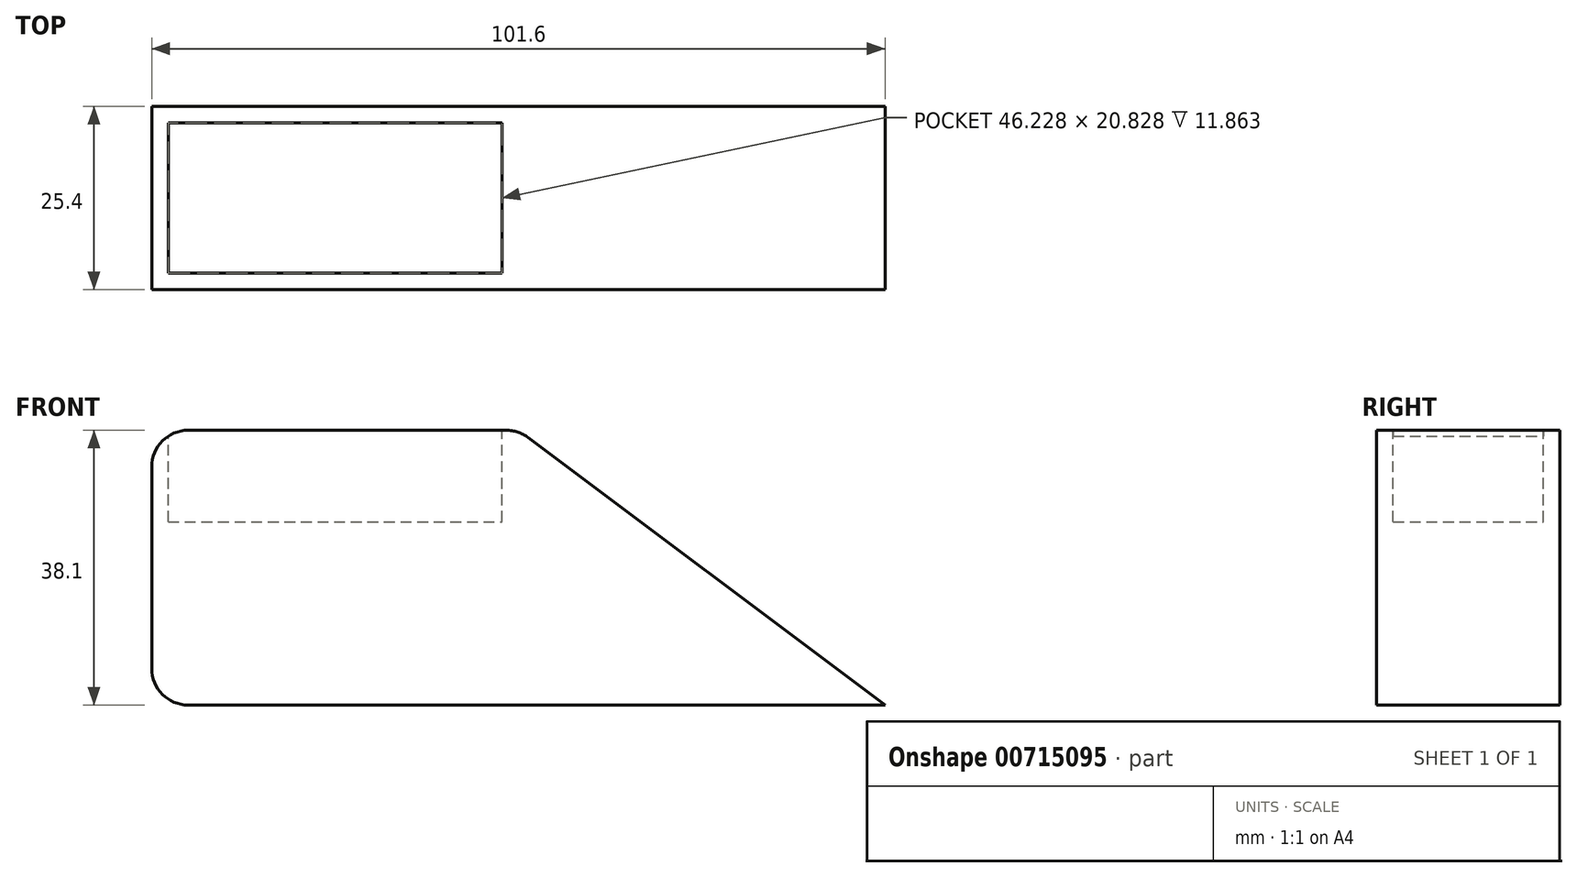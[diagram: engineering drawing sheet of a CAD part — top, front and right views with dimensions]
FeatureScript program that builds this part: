
annotation { "Feature Type Name" : "Feature", "Feature Type Description" : "" }
export const myFeature = defineFeature(function(context is Context, id is Id, definition is map)
    precondition{}
    {
        {
            var Q0;
            Q0=qCreatedBy(makeId("Front.planeOp"),FACE);
            var sketch = newSketch(context, id + "F0", { "sketchPlane" : qUnion([Q0])});
            skLineSegment(sketch, "E0", {"start": v(0, 0) * mm, "end": v(0, 38.1) * mm});
            skLineSegment(sketch, "E1", {"start": v(0, 0) * mm, "end": v(101.6, 0) * mm});
            skLineSegment(sketch, "E2", {"start": v(0, 38.1) * mm, "end": v(50.8, 38.1) * mm});
            skLineSegment(sketch, "E3", {"start": v(50.8, 38.1) * mm, "end": v(101.6, 0) * mm});
            skSolve(sketch);
        }
        {
            var Q0;
            Q0=makeQuery(id+"F0.imprint","IMPRINT",FACE,{"disambiguationData":[TD([[makeQuery(id+"F0.imprint","IMPRINT",EDGE,{"derivedFrom":sQuery(id+"F0.wireOp",EDGE,"E0")}),-1.0]])]});
            extrude(context, id + "F1", {"entities" : qUnion([Q0]), "depth" : 25.4 * mm, "offsetDistance" : 25.4 * mm});
        }
        {
            var Q0;
            Q0=makeQuery(id+"F1.opExtrude","SWEPT_FACE",FACE,{"disambiguationData":[OSD([sQuery(id+"F0.wireOp",EDGE,"E2")])]});
            var sketch = newSketch(context, id + "F2", { "sketchPlane" : qUnion([Q0])});
            skLineSegment(sketch, "E4.bottom", {"start": v(2.29, -23.11) * mm, "end": v(48.51, -23.11) * mm});
            skLineSegment(sketch, "E4.top", {"start": v(2.29, -2.29) * mm, "end": v(48.51, -2.29) * mm});
            skLineSegment(sketch, "E4.left", {"start": v(2.29, -23.11) * mm, "end": v(2.29, -2.29) * mm});
            skLineSegment(sketch, "E4.right", {"start": v(48.51, -23.11) * mm, "end": v(48.51, -2.29) * mm});
            skSolve(sketch);
        }
        {
            var Q0;
            Q0=makeQuery(id+"F2.imprint","IMPRINT",FACE,{"disambiguationData":[TD([[makeQuery(id+"F2.imprint","IMPRINT",EDGE,{"derivedFrom":sQuery(id+"F2.wireOp",EDGE,"E4.bottom")}),1.0]])]});
            extrude(context, id + "F3", {"entities" : qUnion([Q0]), "operationType" : NewBodyOperationType.REMOVE, "oppositeDirection" : true, "depth" : 12.7 * mm, "offsetDistance" : 25.4 * mm});
        }
        {
            var Q0;
            Q0=makeQuery(id+"F1.opExtrude","SWEPT_EDGE",EDGE,{"disambiguationData":[OSD([sQuery(id+"F0.wireOp",EDGE,"E0"),sQuery(id+"F0.wireOp",EDGE,"E2")])]});
            var Q1;
            Q1=makeQuery(id+"F1.opExtrude","SWEPT_EDGE",EDGE,{"disambiguationData":[OSD([sQuery(id+"F0.wireOp",EDGE,"E2"),sQuery(id+"F0.wireOp",EDGE,"E3")])]});
            var Q2;
            Q2=makeQuery(id+"F1.opExtrude","SWEPT_EDGE",EDGE,{"disambiguationData":[OSD([sQuery(id+"F0.wireOp",EDGE,"E0"),sQuery(id+"F0.wireOp",EDGE,"E1")])]});
            fillet(context, id + "F4", {"entities" : qUnion([Q0, Q1, Q2]), "radius" : 5.08 * mm, "tangentPropagation" : true, "allowEdgeOverflow" : false});
        }
    });
